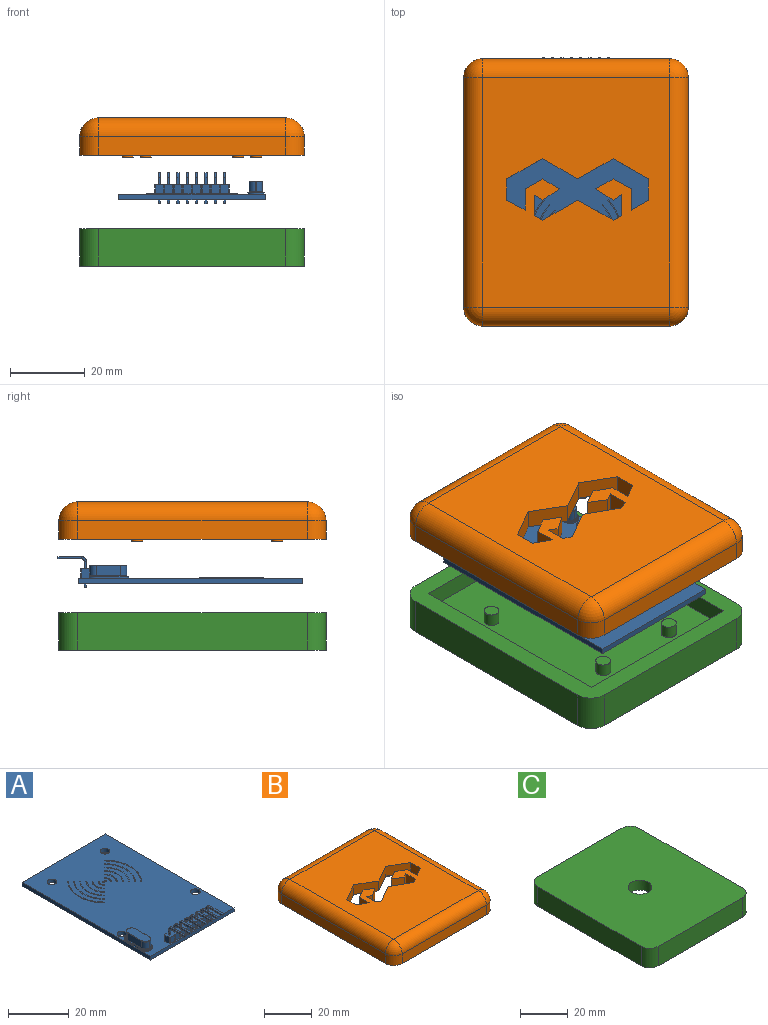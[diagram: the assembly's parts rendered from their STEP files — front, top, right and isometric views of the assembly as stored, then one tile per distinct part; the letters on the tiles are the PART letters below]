
ASSEMBLY  parts=3 mates=2
PART A: 317 faces, bbox 39.2x65.5x8.3 mm
  f0: plane 59.9x39.2mm, normal (0,0,1), area 2181.7mm2, adj f2,f3,f4,f5,f7,f8,f9,f10
  f1: plane 10.8x4.2mm, normal (0,0,1), area 7.3mm2, adj f231,f232,f233,f234,f235,f236,f237,f238
  f2: plane 59.9x1.5mm, normal (1,0,0), area 89.8mm2, adj f0,f3,f5,f6
  f3: plane 39.2x1.5mm, normal (0,1,0), area 58.8mm2, adj f0,f2,f4,f6
  f4: plane 59.9x1.5mm, normal (-1,0,0), area 89.8mm2, adj f0,f3,f5,f6
  f5: plane 39.2x1.5mm, normal (0,-1,0), area 58.8mm2, adj f0,f2,f4,f6
  f6: plane 59.9x39.2mm, normal (0,0,-1), area 2313mm2, adj f2,f3,f4,f5,f7,f8,f9,f10
  f7: cylinder r=1.6mm len=3.2mm, axis (0,0,1), area 15.1mm2, adj f0,f6
  f8: cylinder r=1.6mm len=3.2mm, axis (0,0,1), area 15.1mm2, adj f0,f6
  f9: cylinder r=1.6mm len=3.2mm, axis (0,0,1), area 15.1mm2, adj f0,f6
  f10: cylinder r=1.6mm len=3.2mm, axis (0,0,1), area 15.1mm2, adj f0,f6
  f11: cylinder r=0.25mm len=2.5mm, axis (0,0,-1), area 1mm2, adj f0,f12,f60,f61
  f12: plane 2.5x2mm, normal (0,1,0), area 5mm2, adj f0,f11,f13,f61
  f13: cylinder r=0.25mm len=2.5mm, axis (0,0,-1), area 1mm2, adj f0,f12,f14,f61
  f14: plane 2.5x2mm, normal (-1,0,0), area 5mm2, adj f0,f13,f15,f61
  f15: cylinder r=0.25mm len=2.5mm, axis (0,0,-1), area 1mm2, adj f0,f14,f16,f61
  f16: plane 2.5x2mm, normal (0,-1,0), area 5mm2, adj f0,f15,f17,f61
  f17: cylinder r=0.25mm len=2.5mm, axis (0,0,-1), area 1mm2, adj f0,f16,f18,f61
  f18: cylinder r=0.25mm len=2.5mm, axis (0,0,-1), area 1mm2, adj f0,f17,f19,f61
  f19: plane 2.5x2mm, normal (0,-1,0), area 5mm2, adj f0,f18,f20,f61
  f20: cylinder r=0.25mm len=2.5mm, axis (0,0,-1), area 1mm2, adj f0,f19,f21,f61
  f21: cylinder r=0.25mm len=2.5mm, axis (0,0,-1), area 1mm2, adj f0,f20,f22,f61
  f22: plane 2.5x2mm, normal (0,-1,0), area 5mm2, adj f0,f21,f23,f61
  f23: cylinder r=0.25mm len=2.5mm, axis (0,0,-1), area 1mm2, adj f0,f22,f24,f61
  f24: cylinder r=0.25mm len=2.5mm, axis (0,0,-1), area 1mm2, adj f0,f23,f25,f61
  f25: plane 2.5x2mm, normal (0,-1,0), area 5mm2, adj f0,f24,f26,f61
  f26: cylinder r=0.25mm len=2.5mm, axis (0,0,-1), area 1mm2, adj f0,f25,f27,f61
  f27: cylinder r=0.25mm len=2.5mm, axis (0,0,-1), area 1mm2, adj f0,f26,f28,f61
  f28: plane 2.5x2mm, normal (0,-1,0), area 5mm2, adj f0,f27,f29,f61
  f29: cylinder r=0.25mm len=2.5mm, axis (0,0,-1), area 1mm2, adj f0,f28,f30,f61
  f30: cylinder r=0.25mm len=2.5mm, axis (0,0,-1), area 1mm2, adj f0,f29,f31,f61
  f31: plane 2.5x2mm, normal (0,-1,0), area 5mm2, adj f0,f30,f32,f61
  f32: cylinder r=0.25mm len=2.5mm, axis (0,0,-1), area 1mm2, adj f0,f31,f33,f61
  f33: cylinder r=0.25mm len=2.5mm, axis (0,0,-1), area 1mm2, adj f0,f32,f34,f61
  f34: plane 2.5x2mm, normal (0,-1,0), area 5mm2, adj f0,f33,f35,f61
  f35: cylinder r=0.25mm len=2.5mm, axis (0,0,-1), area 1mm2, adj f0,f34,f36,f61
  f36: cylinder r=0.25mm len=2.5mm, axis (0,0,-1), area 1mm2, adj f0,f35,f37,f61
  f37: plane 2.5x2mm, normal (0,-1,0), area 5mm2, adj f0,f36,f38,f61
  f38: cylinder r=0.25mm len=2.5mm, axis (0,0,-1), area 1mm2, adj f0,f37,f39,f61
  f39: plane 2.5x2mm, normal (1,0,0), area 5mm2, adj f0,f38,f40,f61
  f40: cylinder r=0.25mm len=2.5mm, axis (0,0,-1), area 1mm2, adj f0,f39,f41,f61
  f41: plane 2.5x2mm, normal (0,1,0), area 5mm2, adj f0,f40,f42,f61
  f42: cylinder r=0.25mm len=2.5mm, axis (0,0,-1), area 1mm2, adj f0,f41,f43,f61
  f43: cylinder r=0.25mm len=2.5mm, axis (0,0,-1), area 1mm2, adj f0,f42,f44,f61
  f44: plane 2.5x2mm, normal (0,1,0), area 5mm2, adj f0,f43,f45,f61
  f45: cylinder r=0.25mm len=2.5mm, axis (0,0,-1), area 1mm2, adj f0,f44,f46,f61
  f46: cylinder r=0.25mm len=2.5mm, axis (0,0,-1), area 1mm2, adj f0,f45,f47,f61
  f47: plane 2.5x2mm, normal (0,1,0), area 5mm2, adj f0,f46,f48,f61
  f48: cylinder r=0.25mm len=2.5mm, axis (0,0,-1), area 1mm2, adj f0,f47,f49,f61
  f49: cylinder r=0.25mm len=2.5mm, axis (0,0,-1), area 1mm2, adj f0,f48,f50,f61
  f50: plane 2.5x2mm, normal (0,1,0), area 5mm2, adj f0,f49,f51,f61
  f51: cylinder r=0.25mm len=2.5mm, axis (0,0,-1), area 1mm2, adj f0,f50,f52,f61
  f52: cylinder r=0.25mm len=2.5mm, axis (0,0,-1), area 1mm2, adj f0,f51,f53,f61
  f53: plane 2.5x2mm, normal (0,1,0), area 5mm2, adj f0,f52,f54,f61
  f54: cylinder r=0.25mm len=2.5mm, axis (0,0,-1), area 1mm2, adj f0,f53,f55,f61
  f55: cylinder r=0.25mm len=2.5mm, axis (0,0,-1), area 1mm2, adj f0,f54,f56,f61
  f56: plane 2.5x2mm, normal (0,1,0), area 5mm2, adj f0,f55,f57,f61
  f57: cylinder r=0.25mm len=2.5mm, axis (0,0,-1), area 1mm2, adj f0,f56,f58,f61
  f58: cylinder r=0.25mm len=2.5mm, axis (0,0,-1), area 1mm2, adj f0,f57,f59,f61
  f59: plane 2.5x2mm, normal (0,1,0), area 5mm2, adj f0,f58,f60,f61
  f60: cylinder r=0.25mm len=2.5mm, axis (0,0,-1), area 1mm2, adj f0,f11,f59,f61
  f61: plane 20x2.5mm, normal (0,0,1), area 46.7mm2, adj f11,f12,f13,f14,f15,f16,f17,f18
  f62: plane 0.6x0.6mm, normal (0,-1,0), area 0.4mm2, adj f67,f68,f69,f70
  f63: plane 1.3x1.3mm, normal (-1,0,0), area 0.9mm2, adj f64,f66,f67,f72
  f64: cylinder r=1.3mm len=1.3mm, axis (1,0,0), area 1.2mm2, adj f63,f65,f68,f73
  f65: plane 1.3x1.3mm, normal (1,0,0), area 0.9mm2, adj f64,f66,f69,f71
  f66: cylinder r=0.7mm len=0.7mm, axis (1,0,0), area 0.7mm2, adj f63,f65,f70,f74
  f67: plane 6.3x0.6mm, normal (-1,0,0), area 3.8mm2, adj f62,f63,f68,f70
  f68: plane 6.3x0.6mm, normal (0,0,1), area 3.8mm2, adj f62,f64,f67,f69
  f69: plane 6.3x0.6mm, normal (1,0,0), area 3.8mm2, adj f62,f65,f68,f70
  f70: plane 6.3x0.6mm, normal (0,0,-1), area 3.8mm2, adj f62,f66,f67,f69
  f71: plane 2x0.6mm, normal (1,0,0), area 1.2mm2, adj f61,f65,f73,f74
  f72: plane 2x0.6mm, normal (-1,0,0), area 1.2mm2, adj f61,f63,f73,f74
  f73: plane 2x0.6mm, normal (0,1,0), area 1.2mm2, adj f61,f64,f71,f72
  f74: plane 2x0.6mm, normal (0,-1,0), area 1.2mm2, adj f61,f66,f71,f72
  f75: plane 1x0.6mm, normal (0,-1,0), area 0.6mm2, adj f6,f77,f78,f79
  f76: plane 1x0.6mm, normal (0,1,0), area 0.6mm2, adj f6,f77,f78,f79
  f77: plane 1x0.6mm, normal (-1,0,0), area 0.6mm2, adj f6,f75,f76,f79
  f78: plane 1x0.6mm, normal (1,0,0), area 0.6mm2, adj f6,f75,f76,f79
  f79: plane 0.6x0.6mm, normal (0,0,-1), area 0.4mm2, adj f75,f76,f77,f78
  f80: plane 0.6x0.6mm, normal (0,-1,0), area 0.4mm2, adj f85,f86,f87,f88
  f81: plane 1.3x1.3mm, normal (-1,0,0), area 0.9mm2, adj f82,f84,f85,f90
  f82: cylinder r=1.3mm len=1.3mm, axis (1,0,0), area 1.2mm2, adj f81,f83,f86,f91
  f83: plane 1.3x1.3mm, normal (1,0,0), area 0.9mm2, adj f82,f84,f87,f89
  f84: cylinder r=0.7mm len=0.7mm, axis (1,0,0), area 0.7mm2, adj f81,f83,f88,f92
  f85: plane 6.3x0.6mm, normal (-1,0,0), area 3.8mm2, adj f80,f81,f86,f88
  f86: plane 6.3x0.6mm, normal (0,0,1), area 3.8mm2, adj f80,f82,f85,f87
  f87: plane 6.3x0.6mm, normal (1,0,0), area 3.8mm2, adj f80,f83,f86,f88
  f88: plane 6.3x0.6mm, normal (0,0,-1), area 3.8mm2, adj f80,f84,f85,f87
  f89: plane 2x0.6mm, normal (1,0,0), area 1.2mm2, adj f61,f83,f91,f92
  f90: plane 2x0.6mm, normal (-1,0,0), area 1.2mm2, adj f61,f81,f91,f92
  f91: plane 2x0.6mm, normal (0,1,0), area 1.2mm2, adj f61,f82,f89,f90
  f92: plane 2x0.6mm, normal (0,-1,0), area 1.2mm2, adj f61,f84,f89,f90
  f93: plane 1x0.6mm, normal (0,-1,0), area 0.6mm2, adj f6,f95,f96,f97
  f94: plane 1x0.6mm, normal (0,1,0), area 0.6mm2, adj f6,f95,f96,f97
  f95: plane 1x0.6mm, normal (-1,0,0), area 0.6mm2, adj f6,f93,f94,f97
  f96: plane 1x0.6mm, normal (1,0,0), area 0.6mm2, adj f6,f93,f94,f97
  f97: plane 0.6x0.6mm, normal (0,0,-1), area 0.4mm2, adj f93,f94,f95,f96
  f98: plane 0.6x0.6mm, normal (0,-1,0), area 0.4mm2, adj f103,f104,f105,f106
  f99: plane 1.3x1.3mm, normal (-1,0,0), area 0.9mm2, adj f100,f102,f103,f108
  f100: cylinder r=1.3mm len=1.3mm, axis (1,0,0), area 1.2mm2, adj f99,f101,f104,f109
  f101: plane 1.3x1.3mm, normal (1,0,0), area 0.9mm2, adj f100,f102,f105,f107
  f102: cylinder r=0.7mm len=0.7mm, axis (1,0,0), area 0.7mm2, adj f99,f101,f106,f110
  f103: plane 6.3x0.6mm, normal (-1,0,0), area 3.8mm2, adj f98,f99,f104,f106
  f104: plane 6.3x0.6mm, normal (0,0,1), area 3.8mm2, adj f98,f100,f103,f105
  f105: plane 6.3x0.6mm, normal (1,0,0), area 3.8mm2, adj f98,f101,f104,f106
  f106: plane 6.3x0.6mm, normal (0,0,-1), area 3.8mm2, adj f98,f102,f103,f105
  f107: plane 2x0.6mm, normal (1,0,0), area 1.2mm2, adj f61,f101,f109,f110
  f108: plane 2x0.6mm, normal (-1,0,0), area 1.2mm2, adj f61,f99,f109,f110
  f109: plane 2x0.6mm, normal (0,1,0), area 1.2mm2, adj f61,f100,f107,f108
  f110: plane 2x0.6mm, normal (0,-1,0), area 1.2mm2, adj f61,f102,f107,f108
  f111: plane 1x0.6mm, normal (0,-1,0), area 0.6mm2, adj f6,f113,f114,f115
  f112: plane 1x0.6mm, normal (0,1,0), area 0.6mm2, adj f6,f113,f114,f115
  f113: plane 1x0.6mm, normal (-1,0,0), area 0.6mm2, adj f6,f111,f112,f115
  f114: plane 1x0.6mm, normal (1,0,0), area 0.6mm2, adj f6,f111,f112,f115
  f115: plane 0.6x0.6mm, normal (0,0,-1), area 0.4mm2, adj f111,f112,f113,f114
  f116: plane 0.6x0.6mm, normal (0,-1,0), area 0.4mm2, adj f121,f122,f123,f124
  f117: plane 1.3x1.3mm, normal (-1,0,0), area 0.9mm2, adj f118,f120,f121,f126
  f118: cylinder r=1.3mm len=1.3mm, axis (1,0,0), area 1.2mm2, adj f117,f119,f122,f127
  f119: plane 1.3x1.3mm, normal (1,0,0), area 0.9mm2, adj f118,f120,f123,f125
  f120: cylinder r=0.7mm len=0.7mm, axis (1,0,0), area 0.7mm2, adj f117,f119,f124,f128
  f121: plane 6.3x0.6mm, normal (-1,0,0), area 3.8mm2, adj f116,f117,f122,f124
  f122: plane 6.3x0.6mm, normal (0,0,1), area 3.8mm2, adj f116,f118,f121,f123
  f123: plane 6.3x0.6mm, normal (1,0,0), area 3.8mm2, adj f116,f119,f122,f124
  f124: plane 6.3x0.6mm, normal (0,0,-1), area 3.8mm2, adj f116,f120,f121,f123
  f125: plane 2x0.6mm, normal (1,0,0), area 1.2mm2, adj f61,f119,f127,f128
  f126: plane 2x0.6mm, normal (-1,0,0), area 1.2mm2, adj f61,f117,f127,f128
  f127: plane 2x0.6mm, normal (0,1,0), area 1.2mm2, adj f61,f118,f125,f126
  f128: plane 2x0.6mm, normal (0,-1,0), area 1.2mm2, adj f61,f120,f125,f126
  f129: plane 1x0.6mm, normal (0,-1,0), area 0.6mm2, adj f6,f131,f132,f133
  f130: plane 1x0.6mm, normal (0,1,0), area 0.6mm2, adj f6,f131,f132,f133
  f131: plane 1x0.6mm, normal (-1,0,0), area 0.6mm2, adj f6,f129,f130,f133
  f132: plane 1x0.6mm, normal (1,0,0), area 0.6mm2, adj f6,f129,f130,f133
  f133: plane 0.6x0.6mm, normal (0,0,-1), area 0.4mm2, adj f129,f130,f131,f132
  f134: plane 0.6x0.6mm, normal (0,-1,0), area 0.4mm2, adj f139,f140,f141,f142
  f135: plane 1.3x1.3mm, normal (-1,0,0), area 0.9mm2, adj f136,f138,f139,f144
  f136: cylinder r=1.3mm len=1.3mm, axis (1,0,0), area 1.2mm2, adj f135,f137,f140,f145
  f137: plane 1.3x1.3mm, normal (1,0,0), area 0.9mm2, adj f136,f138,f141,f143
  f138: cylinder r=0.7mm len=0.7mm, axis (1,0,0), area 0.7mm2, adj f135,f137,f142,f146
  f139: plane 6.3x0.6mm, normal (-1,0,0), area 3.8mm2, adj f134,f135,f140,f142
  f140: plane 6.3x0.6mm, normal (0,0,1), area 3.8mm2, adj f134,f136,f139,f141
  f141: plane 6.3x0.6mm, normal (1,0,0), area 3.8mm2, adj f134,f137,f140,f142
  f142: plane 6.3x0.6mm, normal (0,0,-1), area 3.8mm2, adj f134,f138,f139,f141
  f143: plane 2x0.6mm, normal (1,0,0), area 1.2mm2, adj f61,f137,f145,f146
  f144: plane 2x0.6mm, normal (-1,0,0), area 1.2mm2, adj f61,f135,f145,f146
  f145: plane 2x0.6mm, normal (0,1,0), area 1.2mm2, adj f61,f136,f143,f144
  f146: plane 2x0.6mm, normal (0,-1,0), area 1.2mm2, adj f61,f138,f143,f144
  f147: plane 1x0.6mm, normal (0,-1,0), area 0.6mm2, adj f6,f149,f150,f151
  f148: plane 1x0.6mm, normal (0,1,0), area 0.6mm2, adj f6,f149,f150,f151
  f149: plane 1x0.6mm, normal (-1,0,0), area 0.6mm2, adj f6,f147,f148,f151
  f150: plane 1x0.6mm, normal (1,0,0), area 0.6mm2, adj f6,f147,f148,f151
  f151: plane 0.6x0.6mm, normal (0,0,-1), area 0.4mm2, adj f147,f148,f149,f150
  f152: plane 0.6x0.6mm, normal (0,-1,0), area 0.4mm2, adj f157,f158,f159,f160
  f153: plane 1.3x1.3mm, normal (-1,0,0), area 0.9mm2, adj f154,f156,f157,f162
  f154: cylinder r=1.3mm len=1.3mm, axis (1,0,0), area 1.2mm2, adj f153,f155,f158,f163
  f155: plane 1.3x1.3mm, normal (1,0,0), area 0.9mm2, adj f154,f156,f159,f161
  f156: cylinder r=0.7mm len=0.7mm, axis (1,0,0), area 0.7mm2, adj f153,f155,f160,f164
  f157: plane 6.3x0.6mm, normal (-1,0,0), area 3.8mm2, adj f152,f153,f158,f160
  f158: plane 6.3x0.6mm, normal (0,0,1), area 3.8mm2, adj f152,f154,f157,f159
  f159: plane 6.3x0.6mm, normal (1,0,0), area 3.8mm2, adj f152,f155,f158,f160
  f160: plane 6.3x0.6mm, normal (0,0,-1), area 3.8mm2, adj f152,f156,f157,f159
  f161: plane 2x0.6mm, normal (1,0,0), area 1.2mm2, adj f61,f155,f163,f164
  f162: plane 2x0.6mm, normal (-1,0,0), area 1.2mm2, adj f61,f153,f163,f164
  f163: plane 2x0.6mm, normal (0,1,0), area 1.2mm2, adj f61,f154,f161,f162
  f164: plane 2x0.6mm, normal (0,-1,0), area 1.2mm2, adj f61,f156,f161,f162
  f165: plane 1x0.6mm, normal (0,-1,0), area 0.6mm2, adj f6,f167,f168,f169
  f166: plane 1x0.6mm, normal (0,1,0), area 0.6mm2, adj f6,f167,f168,f169
  f167: plane 1x0.6mm, normal (-1,0,0), area 0.6mm2, adj f6,f165,f166,f169
  f168: plane 1x0.6mm, normal (1,0,0), area 0.6mm2, adj f6,f165,f166,f169
  f169: plane 0.6x0.6mm, normal (0,0,-1), area 0.4mm2, adj f165,f166,f167,f168
  f170: plane 0.6x0.6mm, normal (0,-1,0), area 0.4mm2, adj f175,f176,f177,f178
  f171: plane 1.3x1.3mm, normal (-1,0,0), area 0.9mm2, adj f172,f174,f175,f180
  f172: cylinder r=1.3mm len=1.3mm, axis (1,0,0), area 1.2mm2, adj f171,f173,f176,f181
  f173: plane 1.3x1.3mm, normal (1,0,0), area 0.9mm2, adj f172,f174,f177,f179
  f174: cylinder r=0.7mm len=0.7mm, axis (1,0,0), area 0.7mm2, adj f171,f173,f178,f182
  f175: plane 6.3x0.6mm, normal (-1,0,0), area 3.8mm2, adj f170,f171,f176,f178
  f176: plane 6.3x0.6mm, normal (0,0,1), area 3.8mm2, adj f170,f172,f175,f177
  f177: plane 6.3x0.6mm, normal (1,0,0), area 3.8mm2, adj f170,f173,f176,f178
  f178: plane 6.3x0.6mm, normal (0,0,-1), area 3.8mm2, adj f170,f174,f175,f177
  f179: plane 2x0.6mm, normal (1,0,0), area 1.2mm2, adj f61,f173,f181,f182
  f180: plane 2x0.6mm, normal (-1,0,0), area 1.2mm2, adj f61,f171,f181,f182
  f181: plane 2x0.6mm, normal (0,1,0), area 1.2mm2, adj f61,f172,f179,f180
  f182: plane 2x0.6mm, normal (0,-1,0), area 1.2mm2, adj f61,f174,f179,f180
  f183: plane 1x0.6mm, normal (0,-1,0), area 0.6mm2, adj f6,f185,f186,f187
  f184: plane 1x0.6mm, normal (0,1,0), area 0.6mm2, adj f6,f185,f186,f187
  f185: plane 1x0.6mm, normal (-1,0,0), area 0.6mm2, adj f6,f183,f184,f187
  f186: plane 1x0.6mm, normal (1,0,0), area 0.6mm2, adj f6,f183,f184,f187
  f187: plane 0.6x0.6mm, normal (0,0,-1), area 0.4mm2, adj f183,f184,f185,f186
  f188: plane 0.6x0.6mm, normal (0,-1,0), area 0.4mm2, adj f193,f194,f195,f196
  f189: plane 1.3x1.3mm, normal (-1,0,0), area 0.9mm2, adj f190,f192,f193,f198
  f190: cylinder r=1.3mm len=1.3mm, axis (1,0,0), area 1.2mm2, adj f189,f191,f194,f199
  f191: plane 1.3x1.3mm, normal (1,0,0), area 0.9mm2, adj f190,f192,f195,f197
  f192: cylinder r=0.7mm len=0.7mm, axis (1,0,0), area 0.7mm2, adj f189,f191,f196,f200
  f193: plane 6.3x0.6mm, normal (-1,0,0), area 3.8mm2, adj f188,f189,f194,f196
  f194: plane 6.3x0.6mm, normal (0,0,1), area 3.8mm2, adj f188,f190,f193,f195
  f195: plane 6.3x0.6mm, normal (1,0,0), area 3.8mm2, adj f188,f191,f194,f196
  f196: plane 6.3x0.6mm, normal (0,0,-1), area 3.8mm2, adj f188,f192,f193,f195
  f197: plane 2x0.6mm, normal (1,0,0), area 1.2mm2, adj f61,f191,f199,f200
  f198: plane 2x0.6mm, normal (-1,0,0), area 1.2mm2, adj f61,f189,f199,f200
  f199: plane 2x0.6mm, normal (0,1,0), area 1.2mm2, adj f61,f190,f197,f198
  f200: plane 2x0.6mm, normal (0,-1,0), area 1.2mm2, adj f61,f192,f197,f198
  f201: plane 1x0.6mm, normal (0,-1,0), area 0.6mm2, adj f6,f203,f204,f205
  f202: plane 1x0.6mm, normal (0,1,0), area 0.6mm2, adj f6,f203,f204,f205
  f203: plane 1x0.6mm, normal (-1,0,0), area 0.6mm2, adj f6,f201,f202,f205
  f204: plane 1x0.6mm, normal (1,0,0), area 0.6mm2, adj f6,f201,f202,f205
  f205: plane 0.6x0.6mm, normal (0,0,-1), area 0.4mm2, adj f201,f202,f203,f204
  f206: cylinder r=2.1mm len=2.1mm, axis (0,0,-1), area 1.3mm2, adj f0,f207,f213,f243
  f207: plane 0.4x0.2mm, normal (0,-1,0), area 0.1mm2, adj f0,f206,f208,f241
  f208: cylinder r=2.1mm len=2.1mm, axis (0,0,-1), area 1.3mm2, adj f0,f207,f209,f239
  f209: plane 6.8x0.4mm, normal (1,0,0), area 2.7mm2, adj f0,f208,f210,f240
  f210: cylinder r=2.1mm len=2.1mm, axis (0,0,-1), area 1.3mm2, adj f0,f209,f211,f242
  f211: plane 0.4x0.2mm, normal (0,1,0), area 0.1mm2, adj f0,f210,f212,f244
  f212: cylinder r=2.1mm len=2.1mm, axis (0,0,-1), area 1.3mm2, adj f0,f211,f213,f246
  f213: plane 6.8x0.4mm, normal (-1,0,0), area 2.7mm2, adj f0,f206,f212,f245
  f214: cylinder r=1.7mm len=2.8mm, axis (0,0,-1), area 7.5mm2, adj f215,f221,f227,f235
  f215: plane 2.8x0.1mm, normal (0,-1,0), area 0.3mm2, adj f214,f216,f225,f233
  f216: cylinder r=1.7mm len=2.8mm, axis (0,0,-1), area 7.5mm2, adj f215,f217,f223,f231
  f217: plane 6.5x2.8mm, normal (1,0,0), area 18.2mm2, adj f216,f218,f224,f232
  f218: cylinder r=1.7mm len=2.8mm, axis (0,0,-1), area 7.5mm2, adj f217,f219,f226,f234
  f219: plane 2.8x0.1mm, normal (0,1,0), area 0.3mm2, adj f218,f220,f228,f236
  f220: cylinder r=1.7mm len=2.8mm, axis (0,0,-1), area 7.5mm2, adj f219,f221,f230,f238
  f221: plane 6.5x2.8mm, normal (-1,0,0), area 18.2mm2, adj f214,f220,f229,f237
  f222: plane 9.7x3.3mm, normal (0,0,1), area 29.8mm2, adj f223,f224,f225,f226,f227,f228,f229,f230
  f223: torus R=1.6mm, axis (0,0,1), area 0.4mm2, adj f216,f222,f224,f225
  f224: cylinder r=0.1mm len=6.5mm, axis (0,-1,0), area 1mm2, adj f217,f222,f223,f226
  f225: cylinder r=0.1mm len=0.1mm, axis (-1,0,0), area 0mm2, adj f215,f222,f223,f227
  f226: torus R=1.6mm, axis (0,0,1), area 0.4mm2, adj f218,f222,f224,f228
  f227: torus R=1.6mm, axis (0,0,1), area 0.4mm2, adj f214,f222,f225,f229
  f228: cylinder r=0.1mm len=0.1mm, axis (1,0,0), area 0mm2, adj f219,f222,f226,f230
  f229: cylinder r=0.1mm len=6.5mm, axis (0,1,0), area 1mm2, adj f221,f222,f227,f230
  f230: torus R=1.6mm, axis (0,0,1), area 0.4mm2, adj f220,f222,f228,f229
  f231: torus R=1.8mm, axis (0,0,1), area 0.4mm2, adj f1,f216,f232,f233
  f232: cylinder r=0.1mm len=6.5mm, axis (0,1,0), area 1mm2, adj f1,f217,f231,f234
  f233: cylinder r=0.1mm len=0.1mm, axis (1,0,0), area 0mm2, adj f1,f215,f231,f235
  f234: torus R=1.8mm, axis (0,0,1), area 0.4mm2, adj f1,f218,f232,f236
  f235: torus R=1.8mm, axis (0,0,1), area 0.4mm2, adj f1,f214,f233,f237
  f236: cylinder r=0.1mm len=0.1mm, axis (-1,0,0), area 0mm2, adj f1,f219,f234,f238
  f237: cylinder r=0.1mm len=6.5mm, axis (0,-1,0), area 1mm2, adj f1,f221,f235,f238
  f238: torus R=1.8mm, axis (0,0,1), area 0.4mm2, adj f1,f220,f236,f237
  f239: torus R=2mm, axis (0,0,1), area 0.5mm2, adj f1,f208,f240,f241
  f240: cylinder r=0.1mm len=6.8mm, axis (0,-1,0), area 1.1mm2, adj f1,f209,f239,f242
  f241: cylinder r=0.1mm len=0.2mm, axis (-1,0,0), area 0mm2, adj f1,f207,f239,f243
  f242: torus R=2mm, axis (0,0,1), area 0.5mm2, adj f1,f210,f240,f244
  f243: torus R=2mm, axis (0,0,1), area 0.5mm2, adj f1,f206,f241,f245
  f244: cylinder r=0.1mm len=0.2mm, axis (1,0,0), area 0mm2, adj f1,f211,f242,f246
  f245: cylinder r=0.1mm len=6.8mm, axis (0,1,0), area 1.1mm2, adj f1,f213,f243,f246
  f246: torus R=2mm, axis (0,0,1), area 0.5mm2, adj f1,f212,f244,f245
  f247: cylinder r=12.15mm len=17.18mm, axis (0,0,-1), area 1.9mm2, adj f0,f248,f250,f251
  f248: plane 0.21x0.21mm, normal (0.71,-0.71,0), area 0mm2, adj f0,f247,f249,f251
  f249: cylinder r=11.85mm len=16.76mm, axis (0,0,-1), area 1.9mm2, adj f0,f248,f250,f251
  f250: plane 0.21x0.21mm, normal (0.71,0.71,0), area 0mm2, adj f0,f247,f249,f251
  f251: plane 17.18x3.77mm, normal (0,0,1), area 5.7mm2, adj f247,f248,f249,f250
  f252: plane 0.21x0.21mm, normal (0.71,0.71,0), area 0mm2, adj f0,f253,f255,f256
  f253: cylinder r=10.15mm len=14.35mm, axis (0,0,-1), area 1.6mm2, adj f0,f252,f254,f256
  f254: plane 0.21x0.21mm, normal (0.71,-0.71,0), area 0mm2, adj f0,f253,f255,f256
  f255: cylinder r=9.85mm len=13.93mm, axis (0,0,-1), area 1.5mm2, adj f0,f252,f254,f256
  f256: plane 14.35x3.19mm, normal (0,0,1), area 4.7mm2, adj f252,f253,f254,f255
  f257: plane 0.21x0.21mm, normal (0.71,0.71,0), area 0mm2, adj f0,f258,f260,f261
  f258: cylinder r=8.15mm len=11.53mm, axis (0,0,-1), area 1.3mm2, adj f0,f257,f259,f261
  f259: plane 0.21x0.21mm, normal (0.71,-0.71,0), area 0mm2, adj f0,f258,f260,f261
  f260: cylinder r=7.85mm len=11.1mm, axis (0,0,-1), area 1.2mm2, adj f0,f257,f259,f261
  f261: plane 11.53x2.6mm, normal (0,0,1), area 3.8mm2, adj f257,f258,f259,f260
  f262: plane 0.21x0.21mm, normal (0.71,0.71,0), area 0mm2, adj f0,f263,f265,f266
  f263: cylinder r=6.15mm len=8.7mm, axis (0,0,-1), area 1mm2, adj f0,f262,f264,f266
  f264: plane 0.21x0.21mm, normal (0.71,-0.71,0), area 0mm2, adj f0,f263,f265,f266
  f265: cylinder r=5.85mm len=8.27mm, axis (0,0,-1), area 0.9mm2, adj f0,f262,f264,f266
  f266: plane 8.7x2.01mm, normal (0,0,1), area 2.8mm2, adj f262,f263,f264,f265
  f267: plane 0.21x0.21mm, normal (0.71,0.71,0), area 0mm2, adj f0,f268,f270,f271
  f268: cylinder r=4.15mm len=5.87mm, axis (0,0,-1), area 0.7mm2, adj f0,f267,f269,f271
  f269: plane 0.21x0.21mm, normal (0.71,-0.71,0), area 0mm2, adj f0,f268,f270,f271
  f270: cylinder r=3.85mm len=5.44mm, axis (0,0,-1), area 0.6mm2, adj f0,f267,f269,f271
  f271: plane 5.87x1.43mm, normal (0,0,1), area 1.9mm2, adj f267,f268,f269,f270
  f272: plane 0.21x0.21mm, normal (0.71,0.71,0), area 0mm2, adj f0,f273,f275,f276
  f273: cylinder r=2.15mm len=3.04mm, axis (0,0,-1), area 0.3mm2, adj f0,f272,f274,f276
  f274: plane 0.21x0.21mm, normal (0.71,-0.71,0), area 0mm2, adj f0,f273,f275,f276
  f275: cylinder r=1.85mm len=2.62mm, axis (0,0,-1), area 0.3mm2, adj f0,f272,f274,f276
  f276: plane 3.04x0.84mm, normal (0,0,1), area 0.9mm2, adj f272,f273,f274,f275
  f277: plane 0.21x0.21mm, normal (0.71,0.71,0), area 0mm2, adj f0,f278,f280,f281
  f278: cylinder r=0.65mm len=0.92mm, axis (0,0,-1), area 0.1mm2, adj f0,f277,f279,f281
  f279: plane 0.21x0.21mm, normal (0.71,-0.71,0), area 0mm2, adj f0,f278,f280,f281
  f280: cylinder r=0.35mm len=0.5mm, axis (0,0,-1), area 0.1mm2, adj f0,f277,f279,f281
  f281: plane 0.92x0.4mm, normal (0,0,1), area 0.2mm2, adj f277,f278,f279,f280
  f282: plane 0.21x0.21mm, normal (-0.71,-0.71,0), area 0mm2, adj f0,f283,f285,f286
  f283: cylinder r=0.65mm len=0.92mm, axis (0,0,-1), area 0.1mm2, adj f0,f282,f284,f286
  f284: plane 0.21x0.21mm, normal (-0.71,0.71,0), area 0mm2, adj f0,f283,f285,f286
  f285: cylinder r=0.35mm len=0.5mm, axis (0,0,-1), area 0.1mm2, adj f0,f282,f284,f286
  f286: plane 0.92x0.4mm, normal (0,0,1), area 0.2mm2, adj f282,f283,f284,f285
  f287: plane 0.21x0.21mm, normal (-0.71,-0.71,0), area 0mm2, adj f0,f288,f290,f291
  f288: cylinder r=2.15mm len=3.04mm, axis (0,0,-1), area 0.3mm2, adj f0,f287,f289,f291
  f289: plane 0.21x0.21mm, normal (-0.71,0.71,0), area 0mm2, adj f0,f288,f290,f291
  f290: cylinder r=1.85mm len=2.62mm, axis (0,0,-1), area 0.3mm2, adj f0,f287,f289,f291
  f291: plane 3.04x0.84mm, normal (0,0,1), area 0.9mm2, adj f287,f288,f289,f290
  f292: plane 0.21x0.21mm, normal (-0.71,-0.71,0), area 0mm2, adj f0,f293,f295,f296
  f293: cylinder r=4.15mm len=5.87mm, axis (0,0,-1), area 0.7mm2, adj f0,f292,f294,f296
  f294: plane 0.21x0.21mm, normal (-0.71,0.71,0), area 0mm2, adj f0,f293,f295,f296
  f295: cylinder r=3.85mm len=5.44mm, axis (0,0,-1), area 0.6mm2, adj f0,f292,f294,f296
  f296: plane 5.87x1.43mm, normal (0,0,1), area 1.9mm2, adj f292,f293,f294,f295
  f297: plane 0.21x0.21mm, normal (-0.71,-0.71,0), area 0mm2, adj f0,f298,f300,f301
  f298: cylinder r=6.15mm len=8.7mm, axis (0,0,-1), area 1mm2, adj f0,f297,f299,f301
  f299: plane 0.21x0.21mm, normal (-0.71,0.71,0), area 0mm2, adj f0,f298,f300,f301
  f300: cylinder r=5.85mm len=8.27mm, axis (0,0,-1), area 0.9mm2, adj f0,f297,f299,f301
  f301: plane 8.7x2.01mm, normal (0,0,1), area 2.8mm2, adj f297,f298,f299,f300
  f302: plane 0.21x0.21mm, normal (-0.71,-0.71,0), area 0mm2, adj f0,f303,f305,f306
  f303: cylinder r=8.15mm len=11.53mm, axis (0,0,-1), area 1.3mm2, adj f0,f302,f304,f306
  f304: plane 0.21x0.21mm, normal (-0.71,0.71,0), area 0mm2, adj f0,f303,f305,f306
  f305: cylinder r=7.85mm len=11.1mm, axis (0,0,-1), area 1.2mm2, adj f0,f302,f304,f306
  f306: plane 11.53x2.6mm, normal (0,0,1), area 3.8mm2, adj f302,f303,f304,f305
  f307: plane 0.21x0.21mm, normal (-0.71,-0.71,0), area 0mm2, adj f0,f308,f310,f311
  f308: cylinder r=10.15mm len=14.35mm, axis (0,0,-1), area 1.6mm2, adj f0,f307,f309,f311
  f309: plane 0.21x0.21mm, normal (-0.71,0.71,0), area 0mm2, adj f0,f308,f310,f311
  f310: cylinder r=9.85mm len=13.93mm, axis (0,0,-1), area 1.5mm2, adj f0,f307,f309,f311
  f311: plane 14.35x3.19mm, normal (0,0,1), area 4.7mm2, adj f307,f308,f309,f310
  f312: cylinder r=12.15mm len=17.18mm, axis (0,0,-1), area 1.9mm2, adj f0,f313,f315,f316
  f313: plane 0.21x0.21mm, normal (-0.71,0.71,0), area 0mm2, adj f0,f312,f314,f316
  f314: cylinder r=11.85mm len=16.76mm, axis (0,0,-1), area 1.9mm2, adj f0,f313,f315,f316
  f315: plane 0.21x0.21mm, normal (-0.71,-0.71,0), area 0mm2, adj f0,f312,f314,f316
  f316: plane 17.18x3.77mm, normal (0,0,1), area 5.7mm2, adj f312,f313,f314,f315
PART B: 63 faces, bbox 60x71.4x10.6 mm
  f0: plane 5x4.73mm, normal (-0.49,0.87,0), area 27.2mm2, adj f1,f7,f16,f30
  f1: plane 5x4.41mm, normal (0.52,0.85,0), area 25.8mm2, adj f0,f2,f7,f30
  f2: plane 5x4.41mm, normal (0.56,-0.83,0), area 26.7mm2, adj f1,f7,f17,f30
  f3: plane 5x4.73mm, normal (-0.54,-0.84,0), area 28mm2, adj f4,f7,f24,f30
  f4: plane 5x4.73mm, normal (-0.49,0.87,0), area 27.2mm2, adj f3,f5,f7,f30
  f5: plane 5x4.87mm, normal (0.48,0.88,0), area 27.8mm2, adj f4,f7,f25,f30
  f6: plane 71.4x60mm, normal (0,0,-1), area 1192.5mm2, adj f8,f9,f10,f11,f31,f32,f33,f34
  f7: plane 61.4x50mm, normal (0,0,1), area 2731.5mm2, adj f0,f1,f2,f3,f4,f5,f12,f13
  f8: plane 61.4x5mm, normal (1,0,0), area 307mm2, adj f6,f45,f51,f54
  f9: plane 50x5mm, normal (0,1,0), area 250mm2, adj f6,f48,f52,f54
  f10: plane 61.4x5mm, normal (-1,0,0), area 307mm2, adj f6,f43,f47,f48
  f11: plane 50x5mm, normal (0,-1,0), area 250mm2, adj f6,f43,f45,f46
  f12: plane 9.32x5.46mm, normal (-0.51,-0.86,0), area 54mm2, adj f7,f13,f29,f30
  f13: plane 9.6x5.46mm, normal (0.49,-0.87,0), area 55.2mm2, adj f7,f12,f14,f30
  f14: plane 5.69x5mm, normal (1,0,0), area 28.4mm2, adj f7,f13,f15,f30
  f15: plane 5x4.91mm, normal (0.47,0.88,0), area 27.9mm2, adj f7,f14,f16,f30
  f16: plane 5.64x5mm, normal (-1,0,0), area 28.2mm2, adj f0,f7,f15,f30
  f17: plane 5x2.32mm, normal (-0.51,-0.86,0), area 13.5mm2, adj f2,f7,f18,f30
  f18: plane 5.46x5mm, normal (1,0,0), area 27.3mm2, adj f7,f17,f19,f30
  f19: plane 5x2.32mm, normal (0.48,0.88,0), area 13.2mm2, adj f7,f18,f20,f30
  f20: plane 9.28x5.37mm, normal (-0.5,0.87,0), area 53.6mm2, adj f7,f19,f21,f30
  f21: plane 9.55x5.32mm, normal (0.49,0.87,0), area 54.7mm2, adj f7,f20,f22,f30
  f22: plane 5x2.32mm, normal (-0.43,0.9,0), area 12.8mm2, adj f7,f21,f23,f30
  f23: plane 5.73x5mm, normal (-1,0,0), area 28.7mm2, adj f7,f22,f24,f30
  f24: plane 5x2.32mm, normal (0.54,-0.84,0), area 13.8mm2, adj f3,f7,f23,f30
  f25: plane 5.64x5mm, normal (1,0,0), area 28.2mm2, adj f5,f7,f26,f30
  f26: plane 5x4.55mm, normal (-0.5,0.87,0), area 26.3mm2, adj f7,f25,f27,f30
  f27: plane 5.69x5mm, normal (-1,0,0), area 28.4mm2, adj f7,f26,f28,f30
  f28: plane 9.41x5.37mm, normal (-0.5,-0.87,0), area 54.2mm2, adj f7,f27,f29,f30
  f29: plane 9.55x5.37mm, normal (0.49,-0.87,0), area 54.8mm2, adj f7,f12,f28,f30
  f30: plane 61.4x50mm, normal (0,0,-1), area 2681.2mm2, adj f0,f1,f2,f3,f4,f5,f12,f13
  f31: plane 50x5mm, normal (0,1,0), area 250mm2, adj f6,f30,f32,f34
  f32: plane 61.4x5mm, normal (-1,0,0), area 307mm2, adj f6,f30,f31,f33
  f33: plane 50x5mm, normal (0,-1,0), area 250mm2, adj f6,f30,f32,f34
  f34: plane 61.4x5mm, normal (1,0,0), area 307mm2, adj f6,f30,f31,f33
  f35: cylinder r=2mm len=4mm, axis (0,0,1), area 50.3mm2, adj f30,f36
  f36: plane 4x4mm, normal (0,0,-1), area 5.5mm2, adj f35,f55
  f37: cylinder r=2mm len=4mm, axis (0,0,1), area 50.3mm2, adj f30,f38
  f38: plane 4x4mm, normal (0,0,-1), area 5.5mm2, adj f37,f57
  f39: cylinder r=2mm len=4mm, axis (0,0,1), area 50.3mm2, adj f30,f40
  f40: plane 4x4mm, normal (0,0,-1), area 5.5mm2, adj f39,f59
  f41: cylinder r=2mm len=4mm, axis (0,0,1), area 50.3mm2, adj f30,f42
  f42: plane 4x4mm, normal (0,0,-1), area 5.5mm2, adj f41,f61
  f43: cylinder r=5mm len=5mm, axis (0,0,1), area 39.3mm2, adj f6,f10,f11,f44
  f44: sphere r=5mm, area 39.3mm2, adj f43,f46,f47
  f45: cylinder r=5mm len=5mm, axis (0,0,-1), area 39.3mm2, adj f6,f8,f11,f49
  f46: cylinder r=5mm len=50mm, axis (-1,0,0), area 392.7mm2, adj f7,f11,f44,f49
  f47: cylinder r=5mm len=61.4mm, axis (0,1,0), area 482.2mm2, adj f7,f10,f44,f50
  f48: cylinder r=5mm len=5mm, axis (0,0,-1), area 39.3mm2, adj f6,f9,f10,f50
  f49: sphere r=5mm, area 39.3mm2, adj f45,f46,f51
  f50: sphere r=5mm, area 39.3mm2, adj f47,f48,f52
  f51: cylinder r=5mm len=61.4mm, axis (0,-1,0), area 482.2mm2, adj f7,f8,f49,f53
  f52: cylinder r=5mm len=50mm, axis (1,0,0), area 392.7mm2, adj f7,f9,f50,f53
  f53: sphere r=5mm, area 39.3mm2, adj f51,f52,f54
  f54: cylinder r=5mm len=5mm, axis (0,0,1), area 39.3mm2, adj f6,f8,f9,f53
  f55: cylinder r=1.5mm len=3mm, axis (0,0,1), area 15.1mm2, adj f36,f56
  f56: plane 3x3mm, normal (0,0,-1), area 7.1mm2, adj f55
  f57: cylinder r=1.5mm len=3mm, axis (0,0,1), area 15.1mm2, adj f38,f58
  f58: plane 3x3mm, normal (0,0,-1), area 7.1mm2, adj f57
  f59: cylinder r=1.5mm len=3mm, axis (0,0,1), area 15.1mm2, adj f40,f60
  f60: plane 3x3mm, normal (0,0,-1), area 7.1mm2, adj f59
  f61: cylinder r=1.5mm len=3mm, axis (0,0,1), area 15.1mm2, adj f42,f62
  f62: plane 3x3mm, normal (0,0,-1), area 7.1mm2, adj f61
PART C: 24 faces, bbox 60x71.4x10 mm
  f0: plane 71.4x60mm, normal (0,0,-1), area 1192.5mm2, adj f1,f2,f3,f4,f7,f8,f9,f10
  f1: plane 61.4x10mm, normal (1,0,0), area 614mm2, adj f0,f5,f19,f22
  f2: plane 50x10mm, normal (0,1,0), area 500mm2, adj f0,f5,f19,f20
  f3: plane 61.4x10mm, normal (-1,0,0), area 614mm2, adj f0,f5,f20,f21
  f4: plane 50x10mm, normal (0,-1,0), area 500mm2, adj f0,f5,f21,f22
  f5: plane 71.4x60mm, normal (0,0,1), area 4183.9mm2, adj f1,f2,f3,f4,f19,f20,f21,f22
  f6: plane 61.4x50mm, normal (0,0,-1), area 2941.1mm2, adj f7,f8,f9,f10,f12,f14,f16,f18
  f7: plane 61.4x5mm, normal (1,0,0), area 307mm2, adj f0,f6,f8,f10
  f8: plane 50x5mm, normal (0,-1,0), area 250mm2, adj f0,f6,f7,f9
  f9: plane 61.4x5mm, normal (-1,0,0), area 307mm2, adj f0,f6,f8,f10
  f10: plane 50x5mm, normal (0,1,0), area 250mm2, adj f0,f6,f7,f9
  f11: plane 4x4mm, normal (0,0,-1), area 12.6mm2, adj f12
  f12: cylinder r=2mm len=4mm, axis (0,0,1), area 42.7mm2, adj f6,f11
  f13: plane 4x4mm, normal (0,0,-1), area 12.6mm2, adj f14
  f14: cylinder r=2mm len=4mm, axis (0,0,1), area 42.7mm2, adj f6,f13
  f15: plane 4x4mm, normal (0,0,-1), area 12.6mm2, adj f16
  f16: cylinder r=2mm len=4mm, axis (0,0,1), area 42.7mm2, adj f6,f15
  f17: plane 4x4mm, normal (0,0,-1), area 12.6mm2, adj f18
  f18: cylinder r=2mm len=4mm, axis (0,0,1), area 42.7mm2, adj f6,f17
  f19: cylinder r=5mm len=10mm, axis (0,0,1), area 78.5mm2, adj f0,f1,f2,f5
  f20: cylinder r=5mm len=10mm, axis (0,0,-1), area 78.5mm2, adj f0,f2,f3,f5
  f21: cylinder r=5mm len=10mm, axis (0,0,1), area 78.5mm2, adj f0,f3,f4,f5
  f22: cylinder r=5mm len=10mm, axis (0,0,-1), area 78.5mm2, adj f0,f1,f4,f5
  f23: cylinder r=5mm len=10mm, axis (0,0,-1), area 157.1mm2, adj f5,f6
PLACE A rot(axis=(0,0,-1),180deg) t=(60.19,-63.71,-4.51)mm
PLACE B t=(60.19,-64.17,7.4)mm
PLACE C rot(axis=(0,1,0),180deg) t=(60.19,-64.17,-12.23)mm
MATE cylindrical B.f39 <-> C.f18  axis (0,0,-1) through (72.59,-86.86,6.8)mm
MATE cylindrical A.f8 <-> B.f39  axis (0,0,-1) through (72.59,-86.86,-4.51)mm
